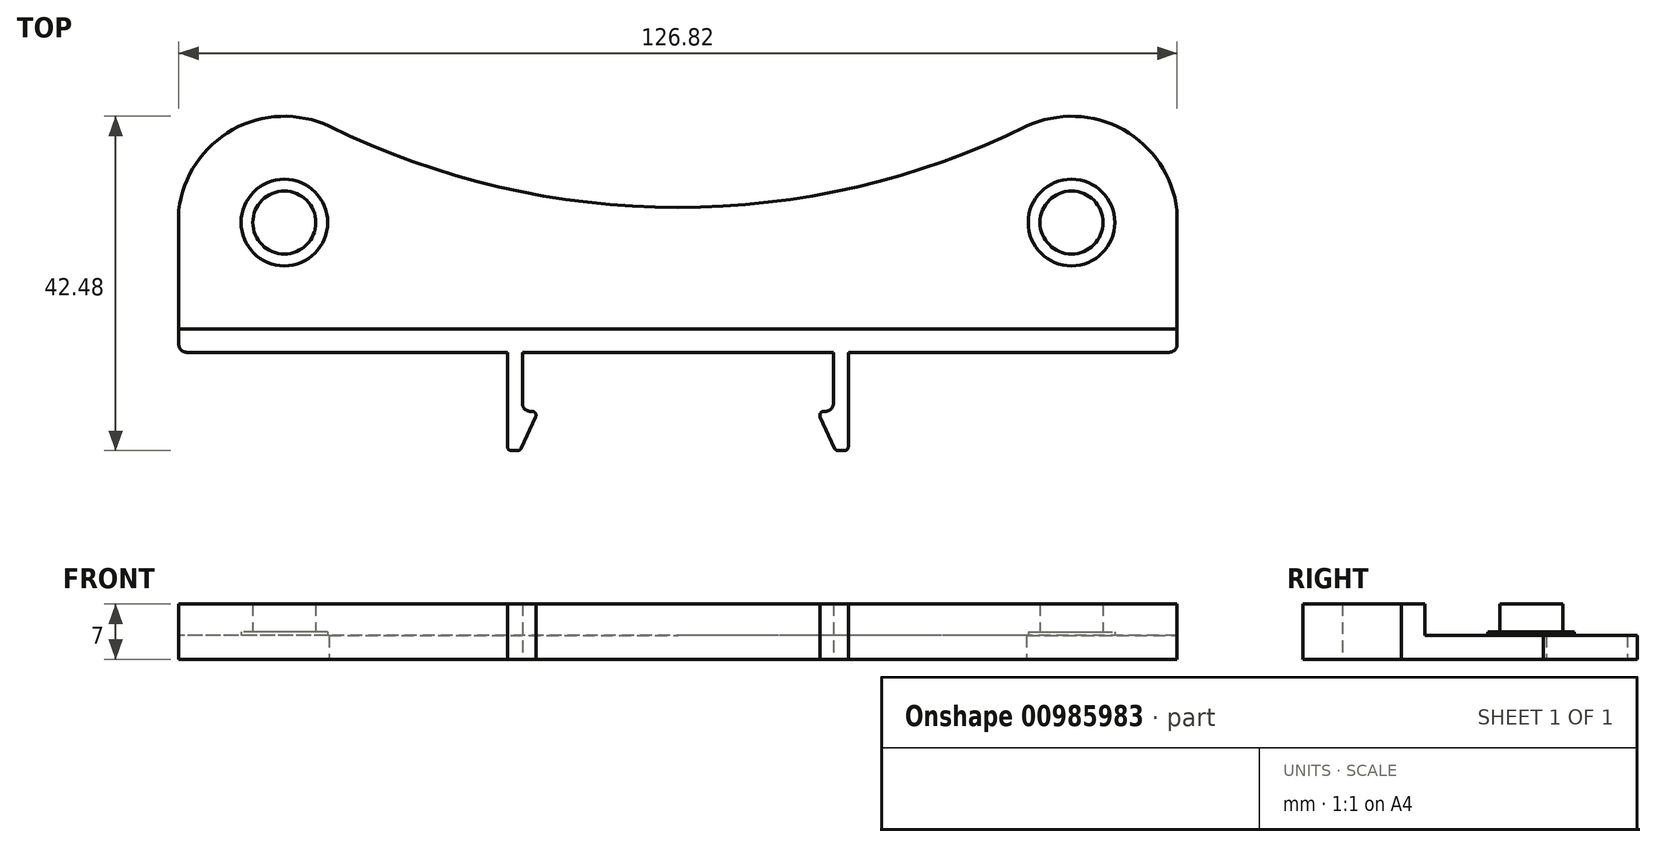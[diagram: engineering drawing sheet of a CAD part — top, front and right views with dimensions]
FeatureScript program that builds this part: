
annotation { "Feature Type Name" : "Feature", "Feature Type Description" : "" }
export const myFeature = defineFeature(function(context is Context, id is Id, definition is map)
    precondition{}
    {
        {
            var Q0;
            Q0=qCreatedBy(makeId("Top.planeOp"),FACE);
            var sketch = newSketch(context, id + "F0", { "sketchPlane" : qUnion([Q0])});
            skPoint(sketch, "E0.0", {"position": v(-63.49, -5.76) * mm});
            skPoint(sketch, "E0.1", {"position": v(-63.4, 9.31) * mm});
            skPoint(sketch, "E0.2", {"position": v(-44.28, 19.97) * mm});
            skPoint(sketch, "E0.3", {"position": v(0, 9.66) * mm});
            skPoint(sketch, "E1.0", {"position": v(-52.35, 10.98) * mm});
            skPoint(sketch, "E1.1", {"position": v(-46.91, 5.2) * mm});
            skPoint(sketch, "E1.2", {"position": v(-52.35, 4.5) * mm});
            skPoint(sketch, "E2.0", {"position": v(-54.1, 4.07) * mm});
            skPoint(sketch, "E2.1", {"position": v(-44.52, 8.3) * mm});
            skPoint(sketch, "E2.2", {"position": v(-51.57, 13.01) * mm});
            skPoint(sketch, "E3.0", {"position": v(-62.06, -8.74) * mm});
            skArc(sketch, "E4", {"start": v(-44.28, 19.97) * mm, "mid": v(-56.57, 19.53) * mm, "end": v(-63.4, 9.31) * mm});
            skArc(sketch, "E5", {"start": v(-44.28, 19.97) * mm, "mid": v(-22.73, 12.26) * mm, "end": v(0, 9.66) * mm});
            skLineSegment(sketch, "E6", {"start": v(-63.4, -8.74) * mm, "end": v(0, -8.74) * mm});
            skCircle(sketch, "E7", {"center": v(-50, 7.74) * mm, "radius": 4 * mm});
            skCircle(sketch, "E8", {"center": v(-50, 7.74) * mm, "radius": 5.5 * mm});
            skLineSegment(sketch, "E9", {"start": v(-21.64, -8.74) * mm, "end": v(-21.64, -21.24) * mm});
            skLineSegment(sketch, "E10", {"start": v(-21.64, -21.24) * mm, "end": v(-20.04, -21.24) * mm});
            skLineSegment(sketch, "E11", {"start": v(-20.04, -21.24) * mm, "end": v(-17.75, -16.24) * mm});
            skLineSegment(sketch, "E12", {"start": v(-17.75, -16.24) * mm, "end": v(-19.75, -16.24) * mm});
            skLineSegment(sketch, "E13", {"start": v(-19.75, -16.24) * mm, "end": v(-19.75, -8.74) * mm});
            skLineSegment(sketch, "E14", {"start": v(0, 9.66) * mm, "end": v(0, -8.74) * mm});
            skLineSegment(sketch, "E15", {"start": v(-63.4, 9.31) * mm, "end": v(-63.4, -8.74) * mm});
            skLineSegment(sketch, "E16", {"start": v(0, -5.76) * mm, "end": v(-63.4, -5.76) * mm});
            skPoint(sketch, "E16.endSnap0", {"position": v(-63.4, -3.17) * mm});
            skPoint(sketch, "E17.orphan", {"position": v(-63.4, -15.65) * mm});
            skSolve(sketch);
        }
        {
            var Q0;
            Q0=makeQuery(id+"F0.imprint","IMPRINT",FACE,{"disambiguationData":[TD([[makeQuery(id+"F0.imprint","IMPRINT",EDGE,{"derivedFrom":sQuery(id+"F0.wireOp",EDGE,"E4")}),1.0]])]});
            extrude(context, id + "F1", {"entities" : qUnion([Q0]), "depth" : 3 * mm, "offsetDistance" : 25 * mm});
        }
        {
            var Q0;
            Q0=makeQuery(id+"F0.imprint","IMPRINT",FACE,{"disambiguationData":[TD([[makeQuery(id+"F0.imprint","IMPRINT",EDGE,{"derivedFrom":sQuery(id+"F0.wireOp",EDGE,"E7")}),-1.0]])]});
            var Q1;
            Q1=sQuery(id+"F0.wireOp",EDGE,"E8");
            extrude(context, id + "F2", {"entities" : qUnion([Q0]), "operationType" : NewBodyOperationType.ADD, "surfaceEntities" : qUnion([Q1]), "depth" : 3.5 * mm, "offsetDistance" : 25 * mm});
        }
        {
            var Q0;
            {var subQ0=sQuery(id+"F0.wireOp",EDGE,"E9");Q0=makeQuery(id+"F0.imprint","IMPRINT",FACE,{"disambiguationData":[TD([[makeQuery(id+"F0.imprint","IMPRINT",EDGE,{"derivedFrom":subQ0}),1.0]])]});}
            var Q1;
            Q1=makeQuery(id+"F0.imprint","IMPRINT",FACE,{"disambiguationData":[TD([[makeQuery(id+"F0.imprint","IMPRINT",EDGE,{"derivedFrom":sQuery(id+"F0.wireOp",EDGE,"E7")}),1.0]])]});
            var Q2;
            {var subQ6=sQuery(id+"F0.wireOp",EDGE,"E16");Q2=makeQuery(id+"F0.imprint","IMPRINT",FACE,{"disambiguationData":[TD([[makeQuery(id+"F0.imprint","IMPRINT",EDGE,{"derivedFrom":subQ6}),1.0]])]});}
            extrude(context, id + "F3", {"entities" : qUnion([Q0, Q1, Q2]), "operationType" : NewBodyOperationType.ADD, "depth" : 7 * mm, "offsetDistance" : 25 * mm});
        }
        {
            var Q0;
            Q0=makeQuery(id+"F3.opExtrude","SWEPT_EDGE",EDGE,{"disambiguationData":[OSD([sQuery(id+"F0.wireOp",EDGE,"E12"),sQuery(id+"F0.wireOp",EDGE,"E13")])]});
            var Q1;
            Q1=makeQuery(id+"F3.opExtrude","SWEPT_EDGE",EDGE,{"disambiguationData":[OSD([sQuery(id+"F0.wireOp",EDGE,"E6"),sQuery(id+"F0.wireOp",EDGE,"E15")])]});
            fillet(context, id + "F4", {"entities" : qUnion([Q0, Q1]), "radius" : 1 * mm, "tangentPropagation" : true, "allowEdgeOverflow" : false});
        }
        {
            var Q0;
            Q0=makeQuery(id+"F3.opExtrude","SWEPT_EDGE",EDGE,{"disambiguationData":[OSD([sQuery(id+"F0.wireOp",EDGE,"E11"),sQuery(id+"F0.wireOp",EDGE,"E12")])]});
            var Q1;
            Q1=makeQuery(id+"F3.opExtrude","SWEPT_EDGE",EDGE,{"disambiguationData":[OSD([sQuery(id+"F0.wireOp",EDGE,"E10"),sQuery(id+"F0.wireOp",EDGE,"E11")])]});
            var Q2;
            Q2=makeQuery(id+"F3.opExtrude","SWEPT_EDGE",EDGE,{"disambiguationData":[OSD([sQuery(id+"F0.wireOp",EDGE,"E9"),sQuery(id+"F0.wireOp",EDGE,"E10")])]});
            fillet(context, id + "F5", {"entities" : qUnion([Q0, Q1, Q2]), "radius" : .5 * mm, "tangentPropagation" : true, "allowEdgeOverflow" : false});
        }
        {
            var Q0;
            Q0=makeQuery(id+"F1.opExtrude","SWEPT_BODY",BODY,{"disambiguationData":[OSD([sQuery(id+"F0.wireOp",EDGE,"E4"),sQuery(id+"F0.wireOp",EDGE,"E5"),sQuery(id+"F0.wireOp",EDGE,"E8"),sQuery(id+"F0.wireOp",EDGE,"E14"),sQuery(id+"F0.wireOp",EDGE,"E15"),sQuery(id+"F0.wireOp",EDGE,"E16")])]});
            var Q1;
            Q1=qCreatedBy(makeId("Right.planeOp"),FACE);
            mirror(context, id + "F6", {"operationType" : NewBodyOperationType.ADD, "entities" : qUnion([Q0]), "mirrorPlane" : qUnion([Q1])});
        }
    });
